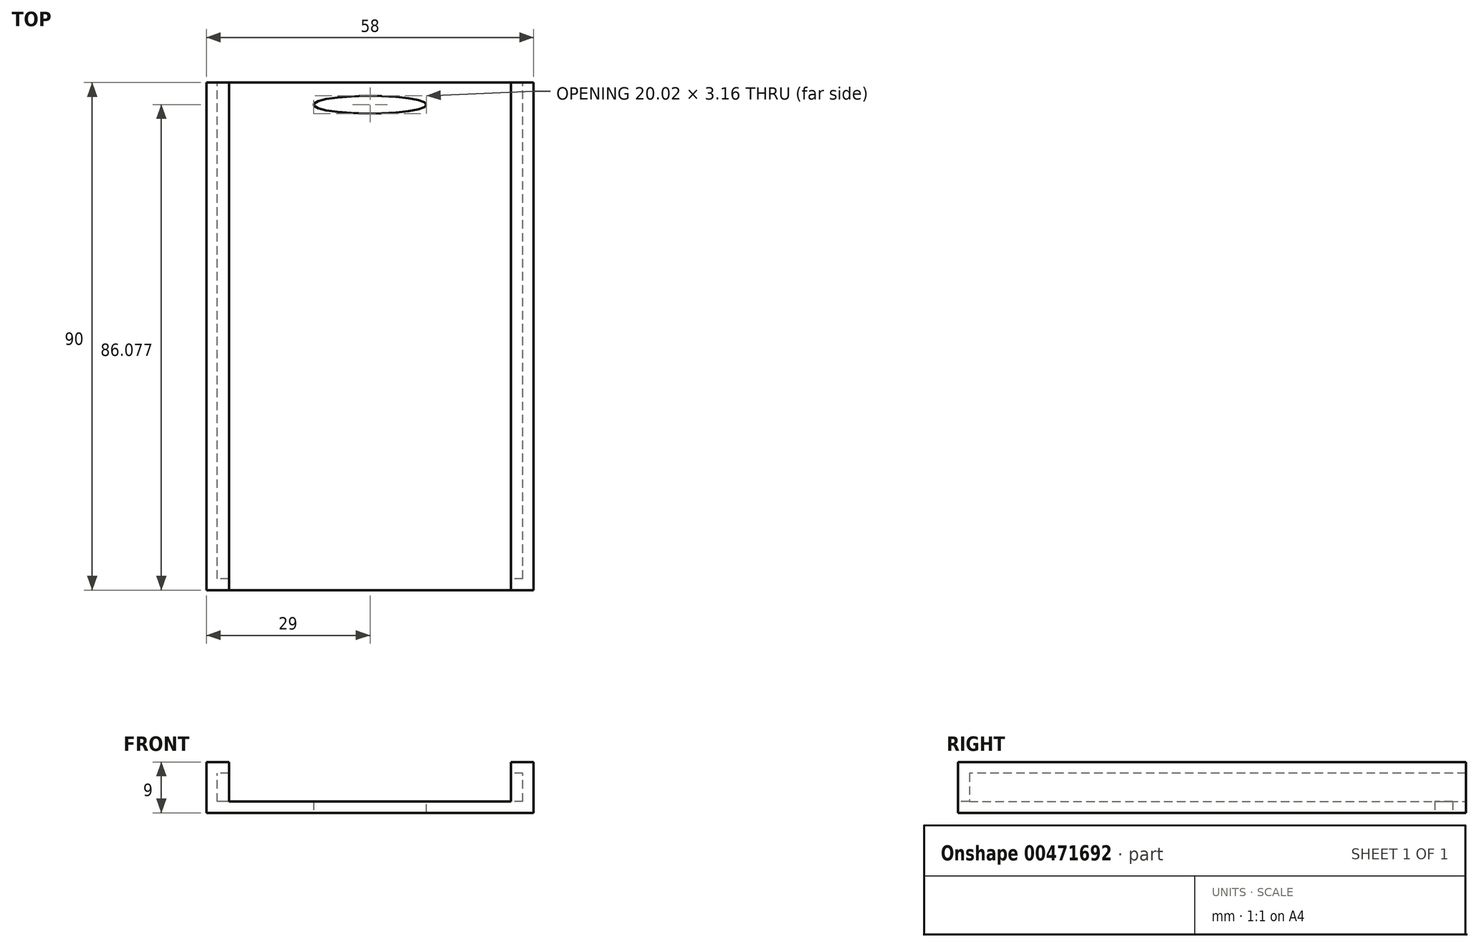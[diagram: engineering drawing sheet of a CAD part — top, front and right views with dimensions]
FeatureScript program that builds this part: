
annotation { "Feature Type Name" : "Feature", "Feature Type Description" : "" }
export const myFeature = defineFeature(function(context is Context, id is Id, definition is map)
    precondition{}
    {
        {
            var Q0;
            Q0=qCreatedBy(makeId("Top.planeOp"),FACE);
            var sketch = newSketch(context, id + "F0", { "sketchPlane" : qUnion([Q0])});
            skLineSegment(sketch, "E0.bottom", {"start": v(29, 45) * mm, "end": v(-29, 45) * mm});
            skLineSegment(sketch, "E0.top", {"start": v(29, -45) * mm, "end": v(-29, -45) * mm});
            skLineSegment(sketch, "E0.left", {"start": v(29, 45) * mm, "end": v(29, -45) * mm});
            skLineSegment(sketch, "E0.right", {"start": v(-29, 45) * mm, "end": v(-29, -45) * mm});
            skPoint(sketch, "E0.middle", {"position": v(0, 0) * mm});
            skSolve(sketch);
        }
        {
            var Q0;
            Q0=makeQuery(id+"F0.imprint","IMPRINT",FACE,{"disambiguationData":[TD([[makeQuery(id+"F0.imprint","IMPRINT",EDGE,{"derivedFrom":sQuery(id+"F0.wireOp",EDGE,"E0.bottom")}),1.0]])]});
            extrude(context, id + "F1", {"entities" : qUnion([Q0]), "depth" : 9 * mm});
        }
        {
            var Q0;
            Q0=makeQuery(id+"F1.opExtrude","CAP_FACE",FACE,{"disambiguationData":[OSD([sQuery(id+"F0.wireOp",EDGE,"E0.bottom"),sQuery(id+"F0.wireOp",EDGE,"E0.top"),sQuery(id+"F0.wireOp",EDGE,"E0.left"),sQuery(id+"F0.wireOp",EDGE,"E0.right")])],"isStart":false});
            var sketch = newSketch(context, id + "F2", { "sketchPlane" : qUnion([Q0])});
            skPoint(sketch, "E1.middle", {"position": v(0, 1) * mm});
            skLineSegment(sketch, "E2.bottom", {"start": v(25, 45) * mm, "end": v(-25, 45) * mm});
            skLineSegment(sketch, "E2.top", {"start": v(25, -45) * mm, "end": v(-25, -45) * mm});
            skLineSegment(sketch, "E2.left", {"start": v(25, 45) * mm, "end": v(25, -45) * mm});
            skLineSegment(sketch, "E2.right", {"start": v(-25, 45) * mm, "end": v(-25, -45) * mm});
            skPoint(sketch, "E2.middle", {"position": v(0, 0) * mm});
            skSolve(sketch);
        }
        {
            var Q0;
            {var subQ0=sQuery(id+"F2.wireOp",EDGE,"E1.top");Q0=makeQuery(id+"F2.imprint","IMPRINT",FACE,{"disambiguationData":[TD([[makeQuery(id+"F2.imprint","IMPRINT",EDGE,{"derivedFrom":subQ0}),-1.0]])]});}
            var Q1;
            Q1=makeQuery(id+"F2.imprint","IMPRINT",FACE,{"disambiguationData":[TD([[makeQuery(id+"F2.imprint","IMPRINT",EDGE,{"derivedFrom":sQuery(id+"F2.wireOp",EDGE,"E2.bottom")}),1.0]])]});
            extrude(context, id + "F3", {"entities" : qUnion([Q0, Q1]), "operationType" : NewBodyOperationType.REMOVE, "oppositeDirection" : true, "depth" : 7 * mm});
        }
        {
            var Q0;
            Q0=makeQuery(id+"F1.opExtrude","SWEPT_FACE",FACE,{"disambiguationData":[OSD([sQuery(id+"F0.wireOp",EDGE,"E0.bottom")])]});
            var sketch = newSketch(context, id + "F4", { "sketchPlane" : qUnion([Q0])});
            skLineSegment(sketch, "E3", {"start": v(-25, 2) * mm, "end": v(-27.1, 2) * mm, "construction": true});
            skLineSegment(sketch, "E4.bottom", {"start": v(-27.1, 2) * mm, "end": v(27.1, 2) * mm});
            skLineSegment(sketch, "E4.top", {"start": v(-27.1, 7) * mm, "end": v(27.1, 7) * mm});
            skLineSegment(sketch, "E4.left", {"start": v(-27.1, 2) * mm, "end": v(-27.1, 7) * mm});
            skLineSegment(sketch, "E4.right", {"start": v(27.1, 2) * mm, "end": v(27.1, 7) * mm});
            skSolve(sketch);
        }
        {
            var Q0;
            Q0 = qSketchRegion(id + "F4", true);
            extrude(context, id + "F5", {"entities" : qUnion([Q0]), "operationType" : NewBodyOperationType.REMOVE, "oppositeDirection" : true, "depth" : 88 * mm});
        }
        {
            var Q0;
            Q0=makeQuery(id+"F3.boolean.opBoolean","COPY",FACE,{"derivedFrom":makeQuery(id+"F3.opExtrude","CAP_FACE",FACE,{"disambiguationData":[OSD([sQuery(id+"F2.wireOp",EDGE,"E2.bottom"),sQuery(id+"F2.wireOp",EDGE,"E2.top"),sQuery(id+"F2.wireOp",EDGE,"E2.left"),sQuery(id+"F2.wireOp",EDGE,"E2.right")])],"isStart":false})});
            var sketch = newSketch(context, id + "F6", { "sketchPlane" : qUnion([Q0])});
            skEllipse(sketch, "E5", {"center": v(0, 41.08) * mm, "majorRadius": 10 * mm, "minorRadius": 1.58 * mm, "majorAxis": v(1, 0)});
            skSolve(sketch);
        }
        {
            var Q0;
            Q0=makeQuery(id+"F6.imprint","IMPRINT",FACE,{"disambiguationData":[TD([[makeQuery(id+"F6.imprint","IMPRINT",EDGE,{"derivedFrom":sQuery(id+"F6.wireOp",EDGE,"E5")}),1.0]])]});
            extrude(context, id + "F7", {"entities" : qUnion([Q0]), "operationType" : NewBodyOperationType.REMOVE, "oppositeDirection" : true, "depth" : 25 * mm});
        }
    });
